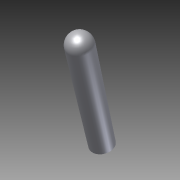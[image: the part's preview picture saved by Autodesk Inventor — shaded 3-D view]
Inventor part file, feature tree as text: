
AUTODESK INVENTOR PART (.ipt)
format: ipt  version: 2011 SP1 (Build 150282100, 282)  size: 92,160 bytes
history: native  units: in
note: dims shown in document units (in); Inventor stores cm internally (conversion verified against a paired STEP export)
features: other x7, revolve x1, sketch x1
ambient origin geometry x8: Origin, YZ Plane, XZ Plane, XY Plane, X Axis, Y Axis, Z Axis, Center Point
bodies: Solid1 (feature_tree)
feature tree (9):
  revolve  "Revolution1"  [1 undecoded]
  other  "bushing_XY"
  other  "bushing_YZ"
  other  "bushing_ZX"
  other  "bushing_X"
  other  "bushing_Y"
  other  "bushing_Z"
  other  "bushing_Center"
  sketch  "Sketch_1"  dims[d0=360.0deg]
note: 1 required parameter value undecoded (feature->parameter linkage not recoverable at this tier; creation-order binding heuristic only, values carry confidence <= 0.55)
